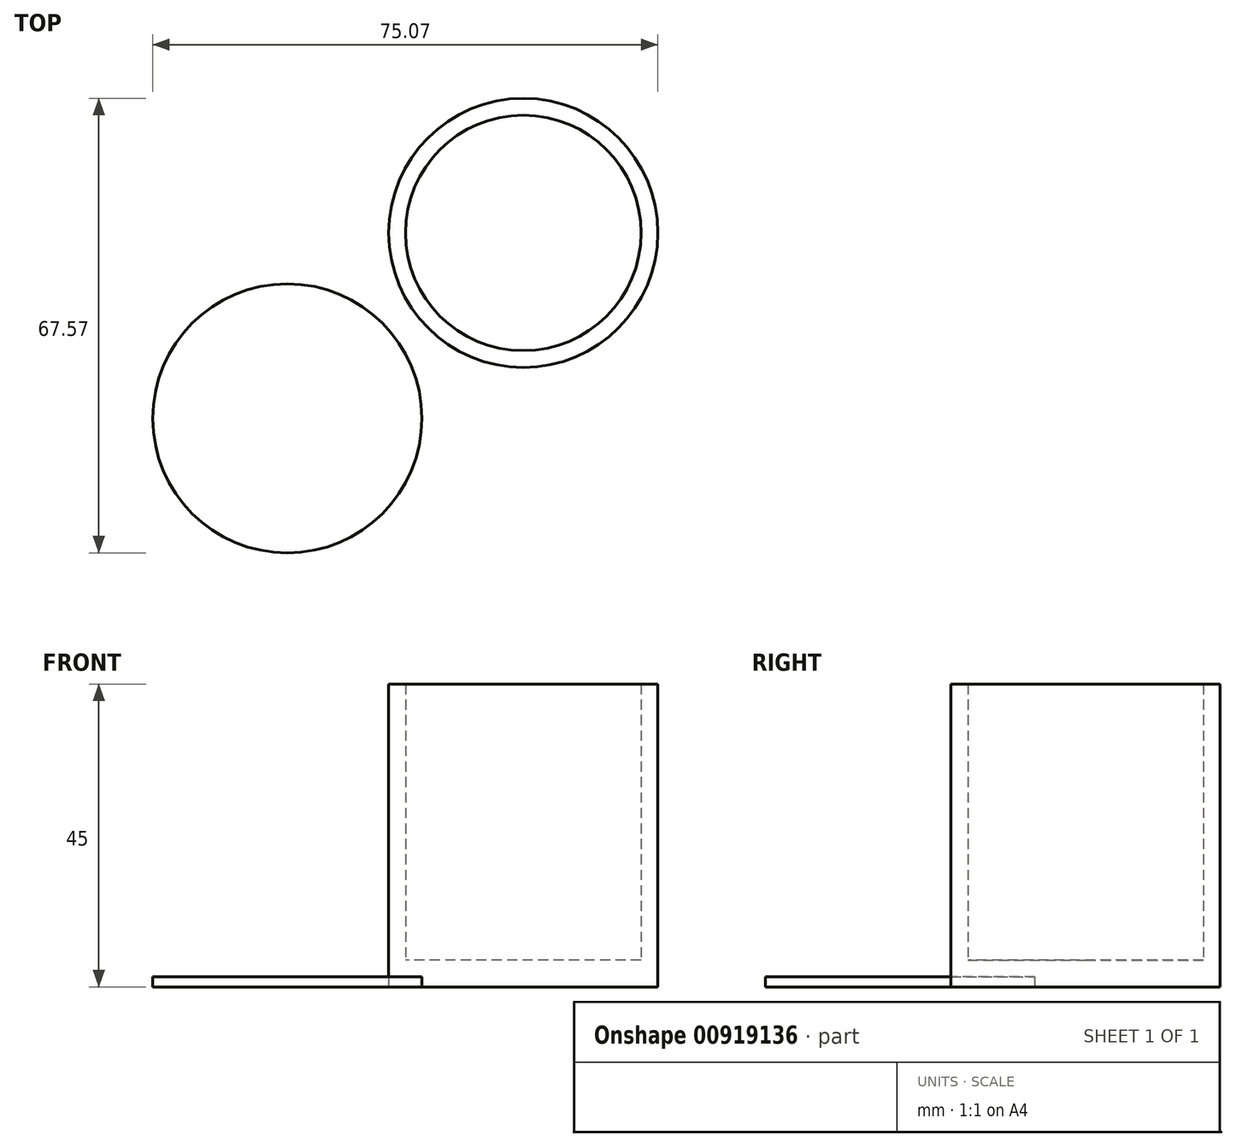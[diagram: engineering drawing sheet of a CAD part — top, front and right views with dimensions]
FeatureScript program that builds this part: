
annotation { "Feature Type Name" : "Feature", "Feature Type Description" : "" }
export const myFeature = defineFeature(function(context is Context, id is Id, definition is map)
    precondition{}
    {
        {
            var Q0;
            Q0=qCreatedBy(makeId("Top.planeOp"),FACE);
            var sketch = newSketch(context, id + "F0", { "sketchPlane" : qUnion([Q0])});
            skCircle(sketch, "E0", {"center": v(0, 0) * mm, "radius": 17.5 * mm});
            skCircle(sketch, "E1", {"center": v(0, 0) * mm, "radius": 20 * mm});
            skCircle(sketch, "E2", {"center": v(-35.07, -27.57) * mm, "radius": 20 * mm});
            skSolve(sketch);
        }
        {
            var Q0;
            Q0=makeQuery(id+"F0.imprint","IMPRINT",FACE,{"disambiguationData":[TD([[makeQuery(id+"F0.imprint","IMPRINT",EDGE,{"derivedFrom":sQuery(id+"F0.wireOp",EDGE,"E2")}),1.0]])]});
            extrude(context, id + "F1", {"entities" : qUnion([Q0]), "depth" : 1.5 * mm, "offsetDistance" : 25 * mm});
        }
        {
            var Q0;
            Q0=makeQuery(id+"F0.imprint","IMPRINT",FACE,{"disambiguationData":[TD([[makeQuery(id+"F0.imprint","IMPRINT",EDGE,{"derivedFrom":sQuery(id+"F0.wireOp",EDGE,"E0")}),1.0]])]});
            extrude(context, id + "F2", {"entities" : qUnion([Q0]), "depth" : 4 * mm, "offsetDistance" : 25 * mm});
        }
        {
            var Q0;
            Q0=makeQuery(id+"F0.imprint","IMPRINT",FACE,{"disambiguationData":[TD([[makeQuery(id+"F0.imprint","IMPRINT",EDGE,{"derivedFrom":sQuery(id+"F0.wireOp",EDGE,"E0")}),-1.0]])]});
            extrude(context, id + "F3", {"entities" : qUnion([Q0]), "operationType" : NewBodyOperationType.ADD, "depth" : 45 * mm, "offsetDistance" : 25 * mm});
        }
    });
